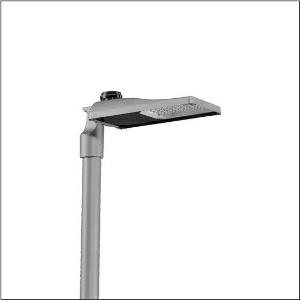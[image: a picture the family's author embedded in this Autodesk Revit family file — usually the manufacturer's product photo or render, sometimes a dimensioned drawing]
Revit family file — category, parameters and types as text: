
# Revit family: streetlight_sl_31_mini___st1_0a_5xh2d3bn08ja_dd0a
name_source: partatom
category: Lighting Fixtures
units: mm (PartAtom-declared; Revit-internal decimal feet)

## family parameters
Cut with Voids When Loaded = No
Host = Face
Light Source = No
Part Type = Normal
Room Calculation Point = No
Round Connector Dimension = Use Diameter
Shared = No

## types (1)
- --- (1 x LED, 12140 lm, 81.1 W, 3000K)
    Apparent Load = 81 VA
    CIE Flux Codes = 40 73 97 100 100
    Color Rendering = 70
    Color Temperature = 3000K
    Default Elevation = 1800 mm
    Description = Streetlight SL 31 mini NEMA (7pin) mast luminaire for post-top, side-entry; light control with lens of PMMA; light distribution: ST1.0a, direct asymmetric distribution, for standard-compliant lighting for roads and squares; LED: luminous flux: 12.140lm, light colour: 730, colour temperature: 3000K; luminous efficacy: 149,7lm/W; control: overheat protection, intelligent temperature release in ECG and LED module, constant luminous flux control, time-dependent luminous flux control, flexible luminous flux parameterisation, pre-setting: linear dimming characteristic; luminaire housing, of diecast aluminium, SITECO metallic grey (DB 702S), corrosivity category C5 high according to DIN EN ISO 12944; cover of toughened safety glass, transparent, mast flange of diecast aluminium, SITECO metallic grey (DB 702S), spigot size: 76/60mm, mast flange included unmounted; cable length: 10,5m, connection cable pre-assembled; mains connection: 220..240V, AC, 50/60Hz; power consumption (at start of service life): 81,1W / (at end of service life): 88,3W / (with reduced operation 50%): 36,4W; protection rating (complete): IP66; insulation class (complete): insulation class I (protective earthing); impact resistance: IK10; certification: CE, ENEC, ENEC+, VDE, UKCA; permissible operating ambient temperature for outdoor applications: -40..+50°C; packaging unit: 1 piece

Light Distribution: ST1.0a
    Height = 76 mm
    Lamp = 1 x LED
    Lamp Light Flux = 12140 lm
    Lamp Power = 81.1 W
    Lamp count = 1
    Length = 547 mm
    Luminous efficacy = 150 lm/W
    Manufacturer = Siteco
    ModVariant = No
    Model = 5XH2D3BN08JA
    Number of Poles = 1
    OnlyDefault = Yes
    Power Factor = 1
    Product Name = Streetlight SL 31 mini | ST1.0a
    Product group = mast luminaire | pylon top
    ProductGroupID = 6100
    Protection Class = Protection class I
    Protection Degree = IP 66
    RLX_Detail_Level = 1
    RLX_Emergency_Light_Flux = 0 lm
    RLX_Emergency_Type = 0
    RLX_Emergency_Type_DB = No
    RlxData = <blob elided: 40217 chars, md5=8ed23541>
    Socket = socket
    Standby Power = 0 W
    System Light Flux = 12140 lm
    System Power = 81 W
    Type Comments = factory setting: luminous flux: 100 % | dim-lin: 254 | 860 mA
    Type Image = l_1300322.jpg
    URL = http://relux.com
    VarID = @adj_057515
    Voltage = 0 V
    Weight = 0.00 kg
    Width = 265 mm

## geometry (parser evidence)
native form markers: Blend x4, Sweep x9
no freeform markers — native parametric forms only
